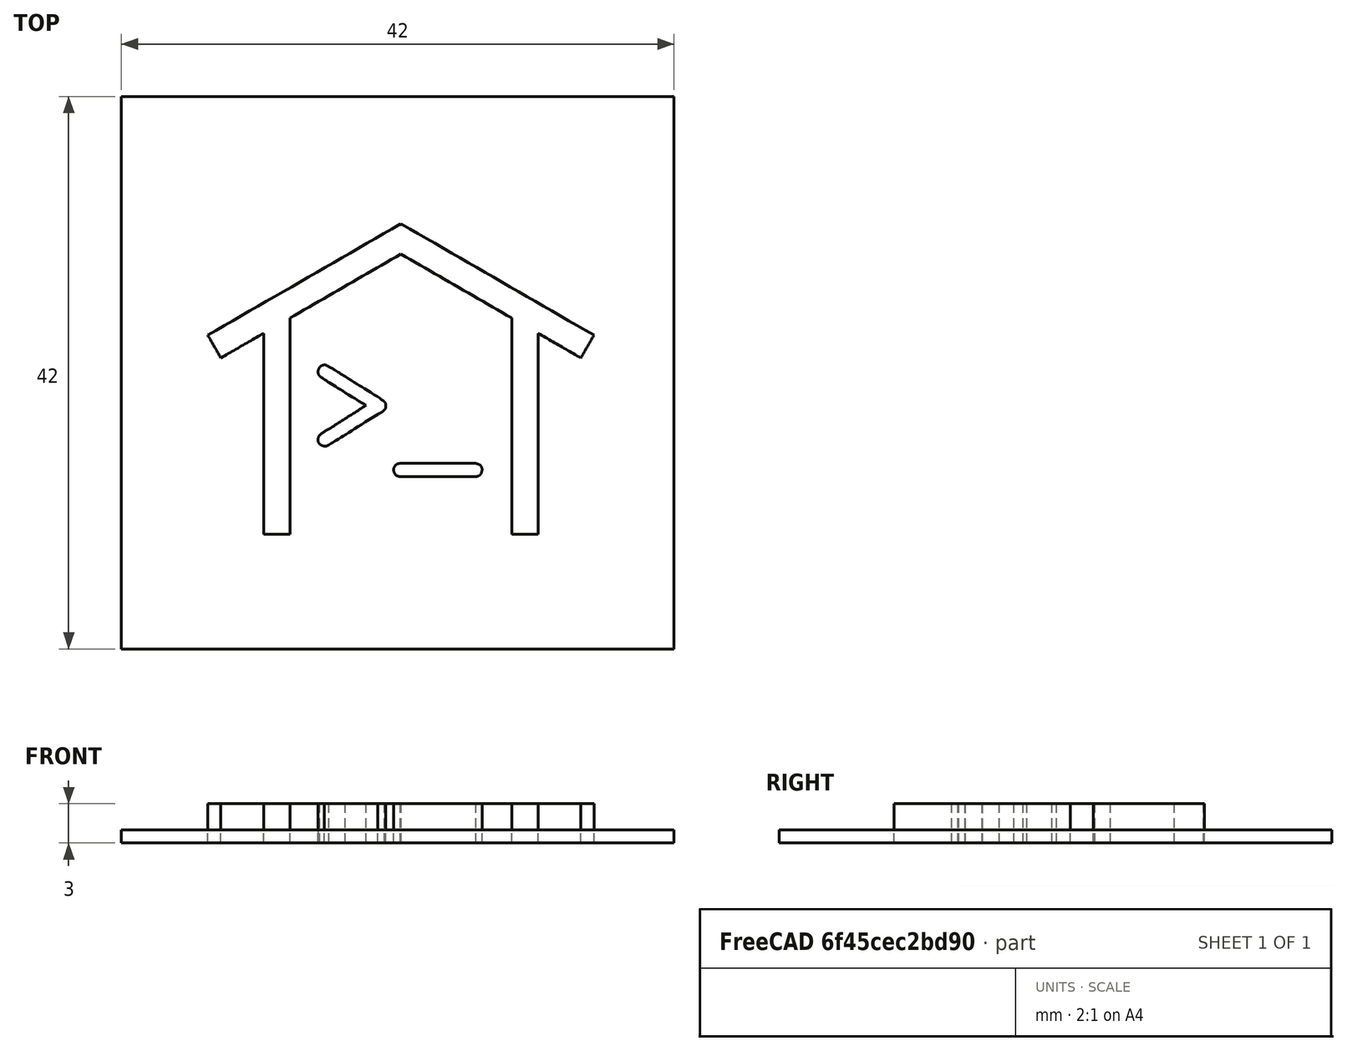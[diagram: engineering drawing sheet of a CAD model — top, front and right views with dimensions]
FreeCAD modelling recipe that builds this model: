
FCSTD DOCUMENT  (FreeCAD 0.16R)
Label: hackerspace-test3d
License: All rights reserved
LicenseURL: http://en.wikipedia.org/wiki/All_rights_reserved
objects: Part::Feature×3, Part::Extrusion×3, Part::Box×1, Part::Compound×1
note: 8 computed .brp shape members not serialized (recipe doc carries the construction recipe); baked Part::Feature solids carry a one-line shape summary decoded from their .brp

FEATURE [Part::Feature] path2994
  shape: bbox 5.165 x 6.183 x 2.585e-07 mm, 0 faces, 0 solids (baked)
FEATURE [Part::Feature] path2996
  shape: bbox 6.737 x 0.9913 x 2.585e-07 mm, 0 faces, 0 solids (baked)
FEATURE [Part::Feature] rect2864_9
  shape: bbox 29.35 x 23.58 x 2e-07 mm, 0 faces, 0 solids (baked)
FEATURE [Part::Extrusion] Extrude
  Base = -> rect2864_9
  Dir = (0,0,3)
  Solid = true
FEATURE [Part::Extrusion] Extrude001
  Base = -> path2994
  Dir = (0,0,3)
  Solid = true
FEATURE [Part::Extrusion] Extrude003
  Base = -> path2996
  Dir = (0,0,3)
  Solid = true
FEATURE [Part::Box] Box  label="Cube"
  Height = 1
  Length = 42
  Placement = pos=(-6,-33,0) rot=(0,0,1;0rad)
  Width = 42
FEATURE [Part::Compound] Compound
  Links = -> [Extrude,Extrude001,Box,Extrude003]
